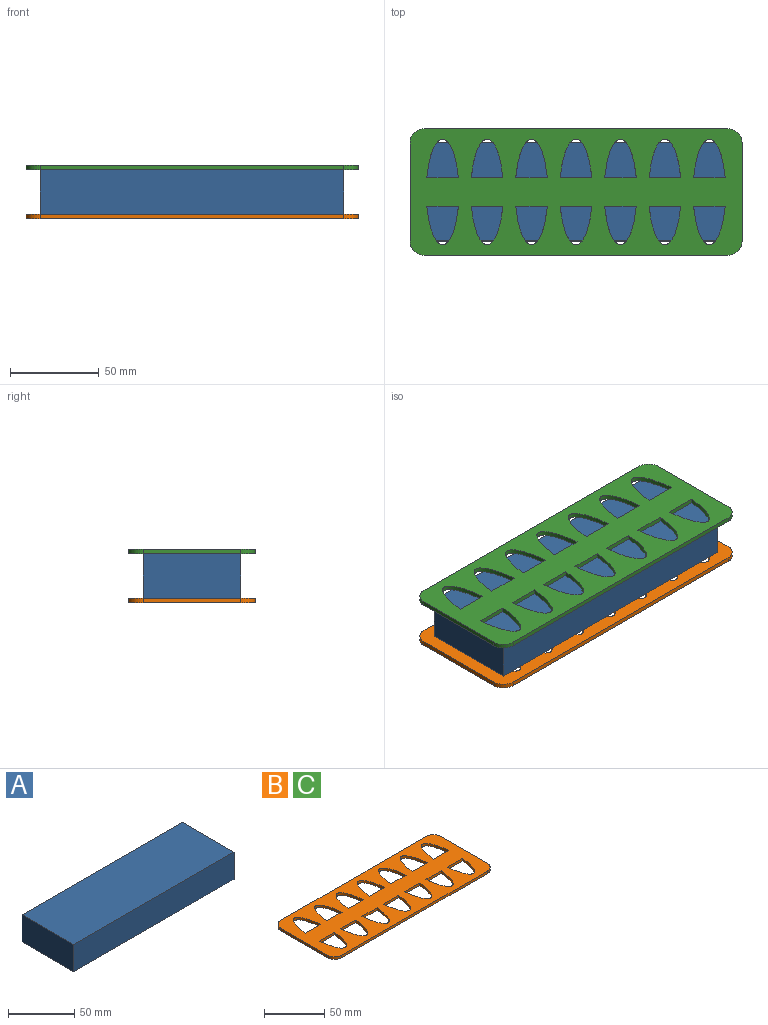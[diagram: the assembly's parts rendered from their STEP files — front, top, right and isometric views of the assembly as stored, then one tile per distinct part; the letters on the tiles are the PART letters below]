
ASSEMBLY  parts=3 mates=2
PART A: 6 faces, bbox 170.6x55.1x25 mm
  f0: plane 55.05x25mm, normal (-1,0,0), area 1376.3mm2, adj f1,f3,f4,f5
  f1: plane 170.65x25mm, normal (0,-1,0), area 4266.2mm2, adj f0,f2,f4,f5
  f2: plane 55.05x25mm, normal (1,0,0), area 1376.3mm2, adj f1,f3,f4,f5
  f3: plane 170.65x25mm, normal (0,1,0), area 4266.2mm2, adj f0,f2,f4,f5
  f4: plane 170.65x55.05mm, normal (0,0,1), area 9394.5mm2, adj f0,f1,f2,f3
  f5: plane 170.65x55.05mm, normal (0,0,-1), area 9394.5mm2, adj f0,f1,f2,f3
PART B: 38 faces, bbox 186.6x71.1x2.5 mm
  f0: extruded ~21.65x17.75mm, area 123.3mm2, adj f15,f16,f37
  f1: extruded ~21.65x17.75mm, area 123.3mm2, adj f15,f16,f34
  f2: extruded ~21.65x17.75mm, area 123.3mm2, adj f15,f16,f32
  f3: extruded ~21.65x17.75mm, area 123.3mm2, adj f15,f16,f30
  f4: extruded ~21.65x17.75mm, area 123.3mm2, adj f15,f16,f28
  f5: extruded ~21.65x17.75mm, area 123.3mm2, adj f15,f16,f26
  f6: extruded ~21.65x17.75mm, area 123.3mm2, adj f15,f16,f24
  f7: cylinder r=8mm len=8mm, axis (0,0,-1), area 31.4mm2, adj f8,f14,f15,f16
  f8: plane 170.65x2.5mm, normal (0,-1,0), area 426.6mm2, adj f7,f9,f15,f16
  f9: cylinder r=8mm len=8mm, axis (0,0,-1), area 31.4mm2, adj f8,f10,f15,f16
  f10: plane 55.05x2.5mm, normal (1,0,0), area 137.6mm2, adj f9,f11,f15,f16
  f11: cylinder r=8mm len=8mm, axis (0,0,-1), area 31.4mm2, adj f10,f12,f15,f16
  f12: plane 170.65x2.5mm, normal (0,1,0), area 426.6mm2, adj f11,f13,f15,f16
  f13: cylinder r=8mm len=8mm, axis (0,0,-1), area 31.4mm2, adj f12,f14,f15,f16
  f14: plane 55.05x2.5mm, normal (-1,0,0), area 137.6mm2, adj f7,f13,f15,f16
  f15: plane 186.65x71.05mm, normal (0,0,1), area 9238.4mm2, adj f0,f1,f2,f3,f4,f5,f6,f7
  f16: plane 186.65x71.05mm, normal (0,0,-1), area 9238.4mm2, adj f0,f1,f2,f3,f4,f5,f6,f7
  f17: extruded ~21.65x17.75mm, area 123.3mm2, adj f15,f16,f36
  f18: extruded ~21.65x17.75mm, area 123.3mm2, adj f15,f16,f35
  f19: extruded ~21.65x17.75mm, area 123.3mm2, adj f15,f16,f33
  f20: extruded ~21.65x17.75mm, area 123.3mm2, adj f15,f16,f31
  f21: extruded ~21.65x17.75mm, area 123.3mm2, adj f15,f16,f29
  f22: extruded ~21.65x17.75mm, area 123.3mm2, adj f15,f16,f27
  f23: extruded ~21.65x17.75mm, area 123.3mm2, adj f15,f16,f25
  f24: plane 17.75x2.5mm, normal (0,-1,0), area 44.4mm2, adj f6,f15,f16
  f25: plane 17.75x2.5mm, normal (0,1,0), area 44.4mm2, adj f15,f16,f23
  f26: plane 17.75x2.5mm, normal (0,-1,0), area 44.4mm2, adj f5,f15,f16
  f27: plane 17.75x2.5mm, normal (0,1,0), area 44.4mm2, adj f15,f16,f22
  f28: plane 17.75x2.5mm, normal (0,-1,0), area 44.4mm2, adj f4,f15,f16
  f29: plane 17.75x2.5mm, normal (0,1,0), area 44.4mm2, adj f15,f16,f21
  f30: plane 17.75x2.5mm, normal (0,-1,0), area 44.4mm2, adj f3,f15,f16
  f31: plane 17.75x2.5mm, normal (0,1,0), area 44.4mm2, adj f15,f16,f20
  f32: plane 17.75x2.5mm, normal (0,-1,0), area 44.4mm2, adj f2,f15,f16
  f33: plane 17.75x2.5mm, normal (0,1,0), area 44.4mm2, adj f15,f16,f19
  f34: plane 17.75x2.5mm, normal (0,-1,0), area 44.4mm2, adj f1,f15,f16
  f35: plane 17.75x2.5mm, normal (0,1,0), area 44.4mm2, adj f15,f16,f18
  f36: plane 17.75x2.5mm, normal (0,1,0), area 44.4mm2, adj f15,f16,f17
  f37: plane 17.75x2.5mm, normal (0,-1,0), area 44.4mm2, adj f0,f15,f16
PART C: same geometry as B
PLACE A t=(0,40.3,0)mm fixed
PLACE B t=(0,40.3,-2.5)mm
PLACE C t=(0,40.3,25)mm
MATE fastened C.f16 <-> A.f4  axis (0,0,-1) through (0,40.3,25)mm
MATE fastened A.f5 <-> B.f15  axis (0,0,-1) through (0,40.3,0)mm
